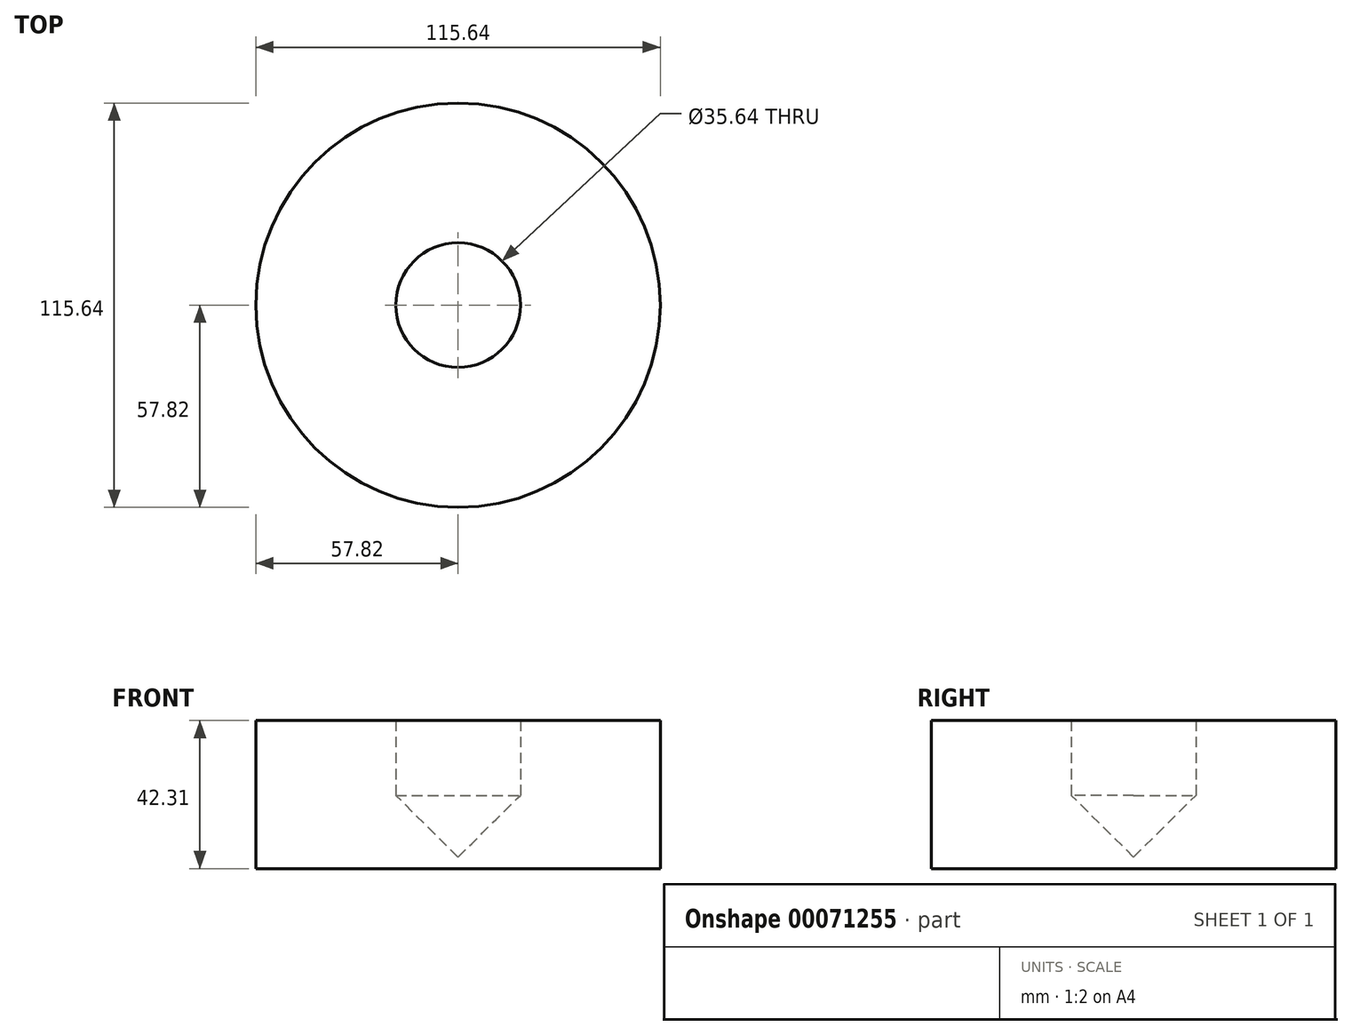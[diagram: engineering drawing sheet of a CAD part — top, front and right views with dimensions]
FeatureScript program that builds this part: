
annotation { "Feature Type Name" : "Feature", "Feature Type Description" : "" }
export const myFeature = defineFeature(function(context is Context, id is Id, definition is map)
    precondition{}
    {
        {
            var Q0;
            Q0=qCreatedBy(makeId("Front.planeOp"),FACE);
            var sketch = newSketch(context, id + "F0", { "sketchPlane" : qUnion([Q0])});
            skLineSegment(sketch, "E0", {"start": v(0, 0) * mm, "end": v(57.82, 0) * mm});
            skLineSegment(sketch, "E1", {"start": v(57.82, 0) * mm, "end": v(57.82, 42.31) * mm});
            skLineSegment(sketch, "E2", {"start": v(57.82, 42.31) * mm, "end": v(17.82, 42.31) * mm});
            skLineSegment(sketch, "E3", {"start": v(17.82, 42.31) * mm, "end": v(17.82, 20.92) * mm});
            skLineSegment(sketch, "E4", {"start": v(17.82, 20.92) * mm, "end": v(0, 3.26) * mm});
            skLineSegment(sketch, "E5", {"start": v(0, 3.26) * mm, "end": v(0, 0) * mm});
            skSolve(sketch);
        }
        {
            var Q0;
            Q0=qCreatedBy(makeId("Front.planeOp"),FACE);
            var sketch = newSketch(context, id + "F1", { "sketchPlane" : qUnion([Q0])});
            skLineSegment(sketch, "E6", {"start": v(0, 0) * mm, "end": v(0, 50.1) * mm});
            skSolve(sketch);
        }
        {
            var Q0;
            Q0=makeQuery(id+"F0.imprint","IMPRINT",FACE,{"disambiguationData":[TD([[makeQuery(id+"F0.imprint","IMPRINT",EDGE,{"derivedFrom":sQuery(id+"F0.wireOp",EDGE,"E0")}),1.0]])]});
            var Q1;
            Q1=sQuery(id+"F1.wireOp",EDGE,"E6");
            revolve(context, id + "F2", {"entities" : qUnion([Q0]), "axis" : qUnion([Q1]), "revolveType" : RevolveType.FULL});
        }
    });
